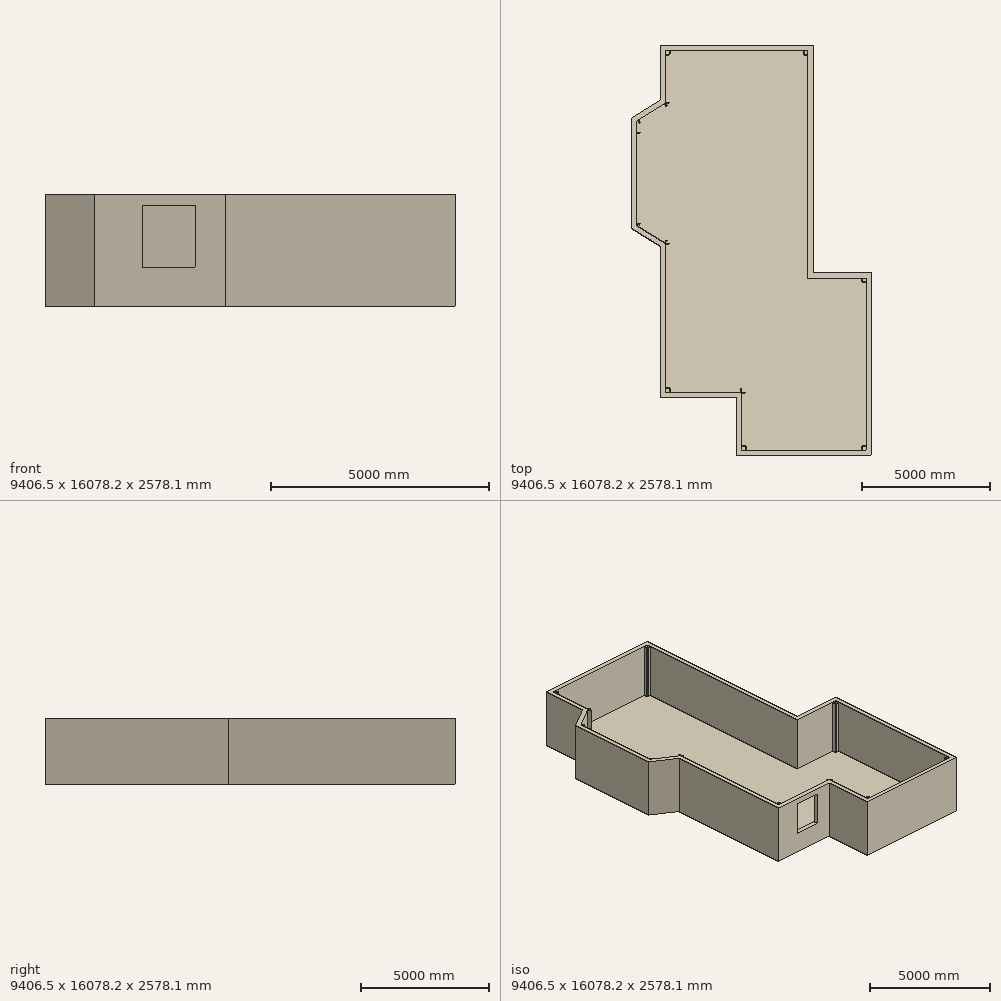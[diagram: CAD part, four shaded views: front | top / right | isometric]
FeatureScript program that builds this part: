
annotation { "Feature Type Name" : "Feature", "Feature Type Description" : "" }
export const myFeature = defineFeature(function(context is Context, id is Id, definition is map)
    precondition{}
    {
        {
            var Q0;
            Q0=qCreatedBy(makeId("Top.planeOp"),FACE);
            var sketch = newSketch(context, id + "F0", { "sketchPlane" : qUnion([Q0])});
            skLineSegment(sketch, "E0", {"start": v(-8280.4, 16078.2) * mm, "end": v(-2286, 16078.2) * mm});
            skLineSegment(sketch, "E1", {"start": v(-2286, 16078.2) * mm, "end": v(-2286, 7162.8) * mm});
            skLineSegment(sketch, "E2", {"start": v(-2286, 7162.8) * mm, "end": v(0, 7162.8) * mm});
            skLineSegment(sketch, "E3", {"start": v(0, 7162.8) * mm, "end": v(0, 0) * mm});
            skLineSegment(sketch, "E4", {"start": v(0, 0) * mm, "end": v(-5283.2, 0) * mm});
            skLineSegment(sketch, "E5", {"start": v(-5283.2, 0) * mm, "end": v(-5283.2, 2286) * mm});
            skLineSegment(sketch, "E6", {"start": v(-5283.2, 2286) * mm, "end": v(-8280.4, 2286) * mm});
            skLineSegment(sketch, "E7", {"start": v(-8280.4, 2286) * mm, "end": v(-8280.4, 8201.03) * mm});
            skLineSegment(sketch, "E8", {"start": v(-8280.4, 8201.03) * mm, "end": v(-9406.5, 8900.32) * mm});
            skLineSegment(sketch, "E9", {"start": v(-9406.5, 8900.32) * mm, "end": v(-9406.5, 13223.08) * mm});
            skLineSegment(sketch, "E10", {"start": v(-9406.5, 13223.08) * mm, "end": v(-8280.4, 13922.38) * mm});
            skLineSegment(sketch, "E11", {"start": v(-8280.4, 13922.38) * mm, "end": v(-8280.4, 16078.2) * mm});
            skSolve(sketch);
        }
        {
            var Q0;
            Q0=qSketchRegion(id+"F0",true);
            extrude(context, id + "F1", {"entities" : qUnion([Q0]), "depth" : 2578.1 * mm});
        }
        {
            var Q0;
            Q0=makeQuery(id+"F1.opExtrude","CAP_FACE",FACE,{"disambiguationData":[OSD([sQuery(id+"F0.wireOp",EDGE,"E0"),sQuery(id+"F0.wireOp",EDGE,"E1"),sQuery(id+"F0.wireOp",EDGE,"E2"),sQuery(id+"F0.wireOp",EDGE,"E3"),sQuery(id+"F0.wireOp",EDGE,"E4"),sQuery(id+"F0.wireOp",EDGE,"E5"),sQuery(id+"F0.wireOp",EDGE,"E6"),sQuery(id+"F0.wireOp",EDGE,"E7"),sQuery(id+"F0.wireOp",EDGE,"E8"),sQuery(id+"F0.wireOp",EDGE,"E9"),sQuery(id+"F0.wireOp",EDGE,"E10"),sQuery(id+"F0.wireOp",EDGE,"E11")])],"isStart":false});
            shell(context, id + "F2", {"entities" : qUnion([Q0]), "thickness" : 203.2 * mm});
        }
        {
            var Q0;
            Q0=makeQuery(id+"F2.opShell","OFFSET_FACE",FACE,{"disambiguationData":[OSD([sQuery(id+"F0.wireOp",EDGE,"E6")])]});
            var sketch = newSketch(context, id + "F3", { "sketchPlane" : qUnion([Q0])});
            skLineSegment(sketch, "E12.bottom", {"start": v(5969, 2324.1) * mm, "end": v(7188.2, 2324.1) * mm});
            skLineSegment(sketch, "E12.top", {"start": v(5969, 901.7) * mm, "end": v(7188.2, 901.7) * mm});
            skLineSegment(sketch, "E12.left", {"start": v(5969, 2324.1) * mm, "end": v(5969, 901.7) * mm});
            skLineSegment(sketch, "E12.right", {"start": v(7188.2, 2324.1) * mm, "end": v(7188.2, 901.7) * mm});
            skPoint(sketch, "E13", {"position": v(6578.6, 2324.1) * mm});
            skSolve(sketch);
        }
        {
            var Q0;
            Q0=makeQuery(id+"F2.opShell","OFFSET_FACE",FACE,{"disambiguationData":[OSD([sQuery(id+"F0.wireOp",EDGE,"E0"),sQuery(id+"F0.wireOp",EDGE,"E1"),sQuery(id+"F0.wireOp",EDGE,"E2"),sQuery(id+"F0.wireOp",EDGE,"E3"),sQuery(id+"F0.wireOp",EDGE,"E4"),sQuery(id+"F0.wireOp",EDGE,"E5"),sQuery(id+"F0.wireOp",EDGE,"E6"),sQuery(id+"F0.wireOp",EDGE,"E7"),sQuery(id+"F0.wireOp",EDGE,"E8"),sQuery(id+"F0.wireOp",EDGE,"E9"),sQuery(id+"F0.wireOp",EDGE,"E10"),sQuery(id+"F0.wireOp",EDGE,"E11")])]});
            var sketch = newSketch(context, id + "F4", { "sketchPlane" : qUnion([Q0])});
            skLineSegment(sketch, "E14.bottom", {"start": v(-8077.2, 13811.9) * mm, "end": v(-7937.5, 13811.9) * mm});
            skLineSegment(sketch, "E14.top", {"start": v(-8077.2, 13850) * mm, "end": v(-7937.5, 13850) * mm});
            skLineSegment(sketch, "E14.left", {"start": v(-8077.2, 13811.9) * mm, "end": v(-8077.2, 13850) * mm});
            skLineSegment(sketch, "E14.right", {"start": v(-7937.5, 13811.9) * mm, "end": v(-7937.5, 13850) * mm});
            skLineSegment(sketch, "E15.bottom", {"start": v(-7934.96, 15875) * mm, "end": v(-7896.86, 15875) * mm});
            skLineSegment(sketch, "E15.top", {"start": v(-7934.96, 15735.3) * mm, "end": v(-7896.86, 15735.3) * mm});
            skLineSegment(sketch, "E15.left", {"start": v(-7934.96, 15875) * mm, "end": v(-7934.96, 15735.3) * mm});
            skLineSegment(sketch, "E15.right", {"start": v(-7896.86, 15875) * mm, "end": v(-7896.86, 15735.3) * mm});
            skLineSegment(sketch, "E16.bottom", {"start": v(-8077.2, 15694.66) * mm, "end": v(-7937.5, 15694.66) * mm});
            skLineSegment(sketch, "E16.top", {"start": v(-8077.2, 15732.76) * mm, "end": v(-7937.5, 15732.76) * mm});
            skLineSegment(sketch, "E16.left", {"start": v(-8077.2, 15694.66) * mm, "end": v(-8077.2, 15732.76) * mm});
            skLineSegment(sketch, "E16.right", {"start": v(-7937.5, 15694.66) * mm, "end": v(-7937.5, 15732.76) * mm});
            skLineSegment(sketch, "E17.bottom", {"start": v(-2631.44, 15875) * mm, "end": v(-2669.54, 15875) * mm});
            skLineSegment(sketch, "E17.top", {"start": v(-2631.44, 15735.3) * mm, "end": v(-2669.54, 15735.3) * mm});
            skLineSegment(sketch, "E17.left", {"start": v(-2631.44, 15875) * mm, "end": v(-2631.44, 15735.3) * mm});
            skLineSegment(sketch, "E17.right", {"start": v(-2669.54, 15875) * mm, "end": v(-2669.54, 15735.3) * mm});
            skLineSegment(sketch, "E18.bottom", {"start": v(-2489.2, 15694.66) * mm, "end": v(-2628.9, 15694.66) * mm});
            skLineSegment(sketch, "E18.top", {"start": v(-2489.2, 15732.76) * mm, "end": v(-2628.9, 15732.76) * mm});
            skLineSegment(sketch, "E18.left", {"start": v(-2489.2, 15694.66) * mm, "end": v(-2489.2, 15732.76) * mm});
            skLineSegment(sketch, "E18.right", {"start": v(-2628.9, 15694.66) * mm, "end": v(-2628.9, 15732.76) * mm});
            skLineSegment(sketch, "E19", {"start": v(-8078.22, 13808.73) * mm, "end": v(-8110.59, 13788.64) * mm});
            skLineSegment(sketch, "E20", {"start": v(-8110.59, 13788.64) * mm, "end": v(-8036.89, 13669.96) * mm});
            skLineSegment(sketch, "E21", {"start": v(-8036.89, 13669.96) * mm, "end": v(-8004.52, 13690.06) * mm});
            skLineSegment(sketch, "E22", {"start": v(-8004.52, 13690.06) * mm, "end": v(-8078.22, 13808.73) * mm});
            skLineSegment(sketch, "E23.bottom", {"start": v(-9203.3, 12669.47) * mm, "end": v(-9063.6, 12669.47) * mm});
            skLineSegment(sketch, "E23.top", {"start": v(-9203.3, 12631.37) * mm, "end": v(-9063.6, 12631.37) * mm});
            skLineSegment(sketch, "E23.left", {"start": v(-9203.3, 12669.47) * mm, "end": v(-9203.3, 12631.37) * mm});
            skLineSegment(sketch, "E23.right", {"start": v(-9063.6, 12669.47) * mm, "end": v(-9063.6, 12631.37) * mm});
            skLineSegment(sketch, "E24", {"start": v(-9162.3, 13135.53) * mm, "end": v(-9129.94, 13155.63) * mm});
            skLineSegment(sketch, "E25", {"start": v(-9129.94, 13155.63) * mm, "end": v(-9056.24, 13036.95) * mm});
            skLineSegment(sketch, "E26", {"start": v(-9056.24, 13036.95) * mm, "end": v(-9088.6, 13016.85) * mm});
            skLineSegment(sketch, "E27", {"start": v(-9088.6, 13016.85) * mm, "end": v(-9162.3, 13135.53) * mm});
            skLineSegment(sketch, "E28", {"start": v(-9162.3, 8987.87) * mm, "end": v(-9088.6, 9106.55) * mm});
            skLineSegment(sketch, "E29", {"start": v(-9088.6, 9106.55) * mm, "end": v(-9056.24, 9086.45) * mm});
            skLineSegment(sketch, "E30", {"start": v(-9056.24, 9086.45) * mm, "end": v(-9129.94, 8967.77) * mm});
            skLineSegment(sketch, "E31", {"start": v(-9129.94, 8967.77) * mm, "end": v(-9162.3, 8987.87) * mm});
            skLineSegment(sketch, "E32", {"start": v(-8109.57, 8334.13) * mm, "end": v(-8077.2, 8314.03) * mm});
            skLineSegment(sketch, "E33", {"start": v(-8077.2, 8314.03) * mm, "end": v(-8003.5, 8432.71) * mm});
            skLineSegment(sketch, "E34", {"start": v(-8003.5, 8432.71) * mm, "end": v(-8035.87, 8452.81) * mm});
            skLineSegment(sketch, "E35", {"start": v(-8035.87, 8452.81) * mm, "end": v(-8109.57, 8334.13) * mm});
            skLineSegment(sketch, "E36.bottom", {"start": v(-9203.3, 9061.59) * mm, "end": v(-9063.6, 9061.59) * mm});
            skLineSegment(sketch, "E36.top", {"start": v(-9203.3, 9099.69) * mm, "end": v(-9063.6, 9099.69) * mm});
            skLineSegment(sketch, "E36.left", {"start": v(-9203.3, 9061.59) * mm, "end": v(-9203.3, 9099.69) * mm});
            skLineSegment(sketch, "E36.right", {"start": v(-9063.6, 9061.59) * mm, "end": v(-9063.6, 9099.69) * mm});
            skLineSegment(sketch, "E37.bottom", {"start": v(-8077.2, 8311.5) * mm, "end": v(-7937.5, 8311.5) * mm});
            skLineSegment(sketch, "E37.top", {"start": v(-8077.2, 8273.4) * mm, "end": v(-7937.5, 8273.4) * mm});
            skLineSegment(sketch, "E37.left", {"start": v(-8077.2, 8311.5) * mm, "end": v(-8077.2, 8273.4) * mm});
            skLineSegment(sketch, "E37.right", {"start": v(-7937.5, 8311.5) * mm, "end": v(-7937.5, 8273.4) * mm});
            skLineSegment(sketch, "E38.bottom", {"start": v(-8077.2, 2631.44) * mm, "end": v(-7937.5, 2631.44) * mm});
            skLineSegment(sketch, "E38.top", {"start": v(-8077.2, 2669.54) * mm, "end": v(-7937.5, 2669.54) * mm});
            skLineSegment(sketch, "E38.left", {"start": v(-8077.2, 2631.44) * mm, "end": v(-8077.2, 2669.54) * mm});
            skLineSegment(sketch, "E38.right", {"start": v(-7937.5, 2631.44) * mm, "end": v(-7937.5, 2669.54) * mm});
            skLineSegment(sketch, "E39.bottom", {"start": v(-7896.86, 2489.2) * mm, "end": v(-7934.96, 2489.2) * mm});
            skLineSegment(sketch, "E39.top", {"start": v(-7896.86, 2628.9) * mm, "end": v(-7934.96, 2628.9) * mm});
            skLineSegment(sketch, "E39.left", {"start": v(-7896.86, 2489.2) * mm, "end": v(-7896.86, 2628.9) * mm});
            skLineSegment(sketch, "E39.right", {"start": v(-7934.96, 2489.2) * mm, "end": v(-7934.96, 2628.9) * mm});
            skLineSegment(sketch, "E40.bottom", {"start": v(-5082.54, 2489.2) * mm, "end": v(-5120.64, 2489.2) * mm});
            skLineSegment(sketch, "E40.top", {"start": v(-5082.54, 2628.9) * mm, "end": v(-5120.64, 2628.9) * mm});
            skLineSegment(sketch, "E40.left", {"start": v(-5082.54, 2489.2) * mm, "end": v(-5082.54, 2628.9) * mm});
            skLineSegment(sketch, "E40.right", {"start": v(-5120.64, 2489.2) * mm, "end": v(-5120.64, 2628.9) * mm});
            skLineSegment(sketch, "E41.top", {"start": v(-5080, 2448.56) * mm, "end": v(-4940.3, 2448.56) * mm});
            skLineSegment(sketch, "E41.right", {"start": v(-4940.3, 2486.66) * mm, "end": v(-4940.3, 2448.56) * mm});
            skLineSegment(sketch, "E42.bottom", {"start": v(-5080, 345.44) * mm, "end": v(-4940.3, 345.44) * mm});
            skLineSegment(sketch, "E42.top", {"start": v(-5080, 383.54) * mm, "end": v(-4940.3, 383.54) * mm});
            skLineSegment(sketch, "E42.left", {"start": v(-5080, 345.44) * mm, "end": v(-5080, 383.54) * mm});
            skLineSegment(sketch, "E42.right", {"start": v(-4940.3, 345.44) * mm, "end": v(-4940.3, 383.54) * mm});
            skLineSegment(sketch, "E43.bottom", {"start": v(-4937.76, 203.2) * mm, "end": v(-4899.66, 203.2) * mm});
            skLineSegment(sketch, "E43.top", {"start": v(-4937.76, 342.9) * mm, "end": v(-4899.66, 342.9) * mm});
            skLineSegment(sketch, "E43.left", {"start": v(-4937.76, 203.2) * mm, "end": v(-4937.76, 342.9) * mm});
            skLineSegment(sketch, "E43.right", {"start": v(-4899.66, 203.2) * mm, "end": v(-4899.66, 342.9) * mm});
            skLineSegment(sketch, "E44.bottom", {"start": v(-383.54, 203.2) * mm, "end": v(-345.44, 203.2) * mm});
            skLineSegment(sketch, "E44.top", {"start": v(-383.54, 342.9) * mm, "end": v(-345.44, 342.9) * mm});
            skLineSegment(sketch, "E44.left", {"start": v(-383.54, 203.2) * mm, "end": v(-383.54, 342.9) * mm});
            skLineSegment(sketch, "E44.right", {"start": v(-345.44, 203.2) * mm, "end": v(-345.44, 342.9) * mm});
            skLineSegment(sketch, "E45.bottom", {"start": v(-203.2, 345.44) * mm, "end": v(-342.9, 345.44) * mm});
            skLineSegment(sketch, "E45.top", {"start": v(-203.2, 383.54) * mm, "end": v(-342.9, 383.54) * mm});
            skLineSegment(sketch, "E45.left", {"start": v(-203.2, 345.44) * mm, "end": v(-203.2, 383.54) * mm});
            skLineSegment(sketch, "E45.right", {"start": v(-342.9, 345.44) * mm, "end": v(-342.9, 383.54) * mm});
            skLineSegment(sketch, "E46.bottom", {"start": v(-203.2, 6779.26) * mm, "end": v(-342.9, 6779.26) * mm});
            skLineSegment(sketch, "E46.top", {"start": v(-203.2, 6817.36) * mm, "end": v(-342.9, 6817.36) * mm});
            skLineSegment(sketch, "E46.left", {"start": v(-203.2, 6779.26) * mm, "end": v(-203.2, 6817.36) * mm});
            skLineSegment(sketch, "E46.right", {"start": v(-342.9, 6779.26) * mm, "end": v(-342.9, 6817.36) * mm});
            skLineSegment(sketch, "E47.bottom", {"start": v(-345.44, 6959.6) * mm, "end": v(-383.54, 6959.6) * mm});
            skLineSegment(sketch, "E47.top", {"start": v(-345.44, 6819.9) * mm, "end": v(-383.54, 6819.9) * mm});
            skLineSegment(sketch, "E47.left", {"start": v(-345.44, 6959.6) * mm, "end": v(-345.44, 6819.9) * mm});
            skLineSegment(sketch, "E47.right", {"start": v(-383.54, 6959.6) * mm, "end": v(-383.54, 6819.9) * mm});
            skLineSegment(sketch, "E48", {"start": v(-4940.3, 2486.66) * mm, "end": v(-5080, 2486.66) * mm});
            skLineSegment(sketch, "E49", {"start": v(-5080, 2486.66) * mm, "end": v(-5080, 2448.56) * mm});
            skLineSegment(sketch, "E50", {"start": v(-9203.3, 13110.07) * mm, "end": v(-9045.7, 12987.43) * mm, "construction": true});
            skLineSegment(sketch, "E51", {"start": v(-9045.7, 12987.43) * mm, "end": v(-9104.83, 13171.22) * mm, "construction": true});
            skLineSegment(sketch, "E52", {"start": v(-9104.83, 13171.22) * mm, "end": v(-9203.3, 12968.55) * mm, "construction": true});
            skLineSegment(sketch, "E53", {"start": v(-9203.3, 12968.55) * mm, "end": v(-9045.7, 12987.43) * mm, "construction": true});
            skSolve(sketch);
        }
        {
            var Q0;
            Q0=qSketchRegion(id+"F3",true);
            var Q1;
            Q1=makeQuery(id+"F7.opExtrude","SWEPT_FACE",FACE,{"disambiguationData":[OSD([sQuery(id+"FoojXG4nMktDod7_1.wireOp",EDGE,"1VciS72g-VBcj-X035-P1CE-B9HJ2LFSvZOH.top"),sQuery(id+"FoojXG4nMktDod7_1.wireOp",EDGE,"icQnHHDd-8pVd-SaWu-tjJm-3fqmfHu7QenC")])]});
            extrude(context, id + "F5", {"entities" : qUnion([Q0]), "operationType" : NewBodyOperationType.REMOVE, "endBound" : BoundingType.UP_TO_NEXT, "oppositeDirection" : true, "depth" : 25.4 * mm});
        }
        {
            var Q0;
            Q0=qSketchRegion(id+"F4",true);
            extrude(context, id + "F6", {"entities" : qUnion([Q0]), "operationType" : NewBodyOperationType.ADD, "depth" : 2349.5 * mm});
        }
    });
